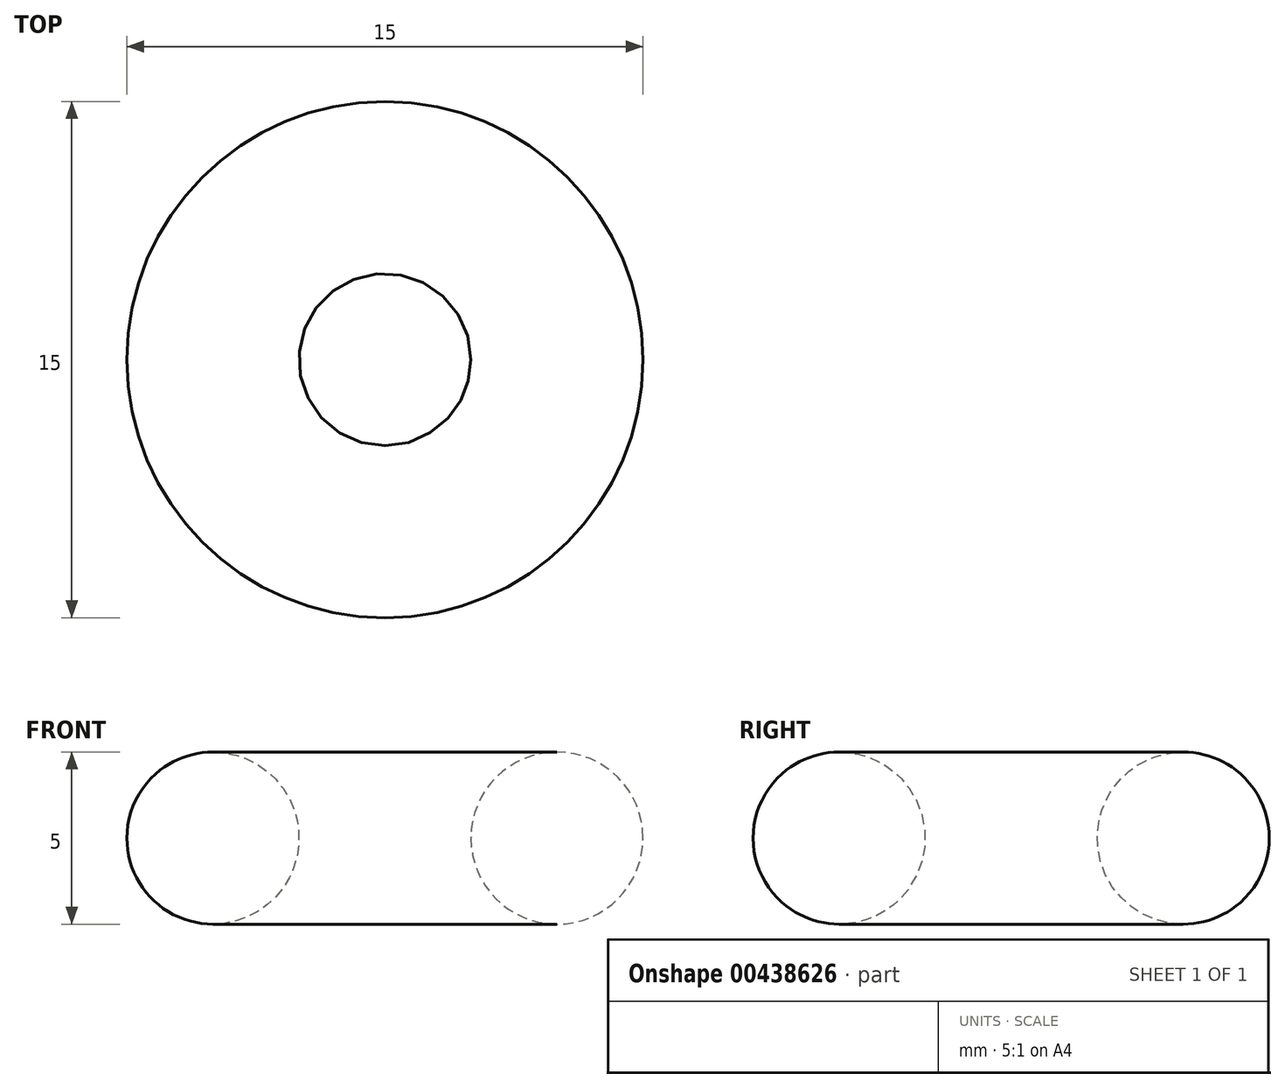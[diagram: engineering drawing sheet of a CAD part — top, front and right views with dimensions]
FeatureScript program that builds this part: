
annotation { "Feature Type Name" : "Feature", "Feature Type Description" : "" }
export const myFeature = defineFeature(function(context is Context, id is Id, definition is map)
    precondition{}
    {
        {
            var Q0;
            Q0=qCreatedBy(makeId("Front.planeOp"),FACE);
            var sketch = newSketch(context, id + "F0", { "sketchPlane" : qUnion([Q0])});
            skLineSegment(sketch, "E0", {"start": v(0, 0) * mm, "end": v(-5, 0) * mm});
            skLineSegment(sketch, "E1", {"start": v(-5, 0) * mm, "end": v(5, 0) * mm});
            skCircle(sketch, "E2", {"center": v(-5, 0) * mm, "radius": 2.5 * mm});
            skCircle(sketch, "E3.MirrorC", {"center": v(5, 0) * mm, "radius": 2.5 * mm});
            skSolve(sketch);
        }
        {
            var Q0;
            Q0=qCreatedBy(makeId("Front.planeOp"),FACE);
            var sketch = newSketch(context, id + "F1", { "sketchPlane" : qUnion([Q0])});
            skLineSegment(sketch, "E4", {"start": v(0, 0) * mm, "end": v(0, 8.3) * mm});
            skLineSegment(sketch, "E5", {"start": v(0, 8.3) * mm, "end": v(0, -13.04) * mm});
            skSolve(sketch);
        }
        {
            var Q0;
            Q0=makeQuery(id+"F0.imprint","IMPRINT",FACE,{"disambiguationData":[TD([[makeQuery(id+"F0.imprint","IMPRINT",EDGE,{"derivedFrom":sQuery(id+"F0.wireOp",EDGE,"E2")}),1.0]])]});
            var Q1;
            Q1=makeQuery(id+"F0.imprint","IMPRINT",FACE,{"disambiguationData":[TD([[makeQuery(id+"F0.imprint","IMPRINT",EDGE,{"derivedFrom":sQuery(id+"F0.wireOp",EDGE,"E3.MirrorC")}),-1.0]])]});
            var Q2;
            Q2=sQuery(id+"F1.wireOp",EDGE,"E5");
            revolve(context, id + "F2", {"entities" : qUnion([Q0, Q1]), "axis" : qUnion([Q2]), "revolveType" : RevolveType.FULL});
        }
    });
